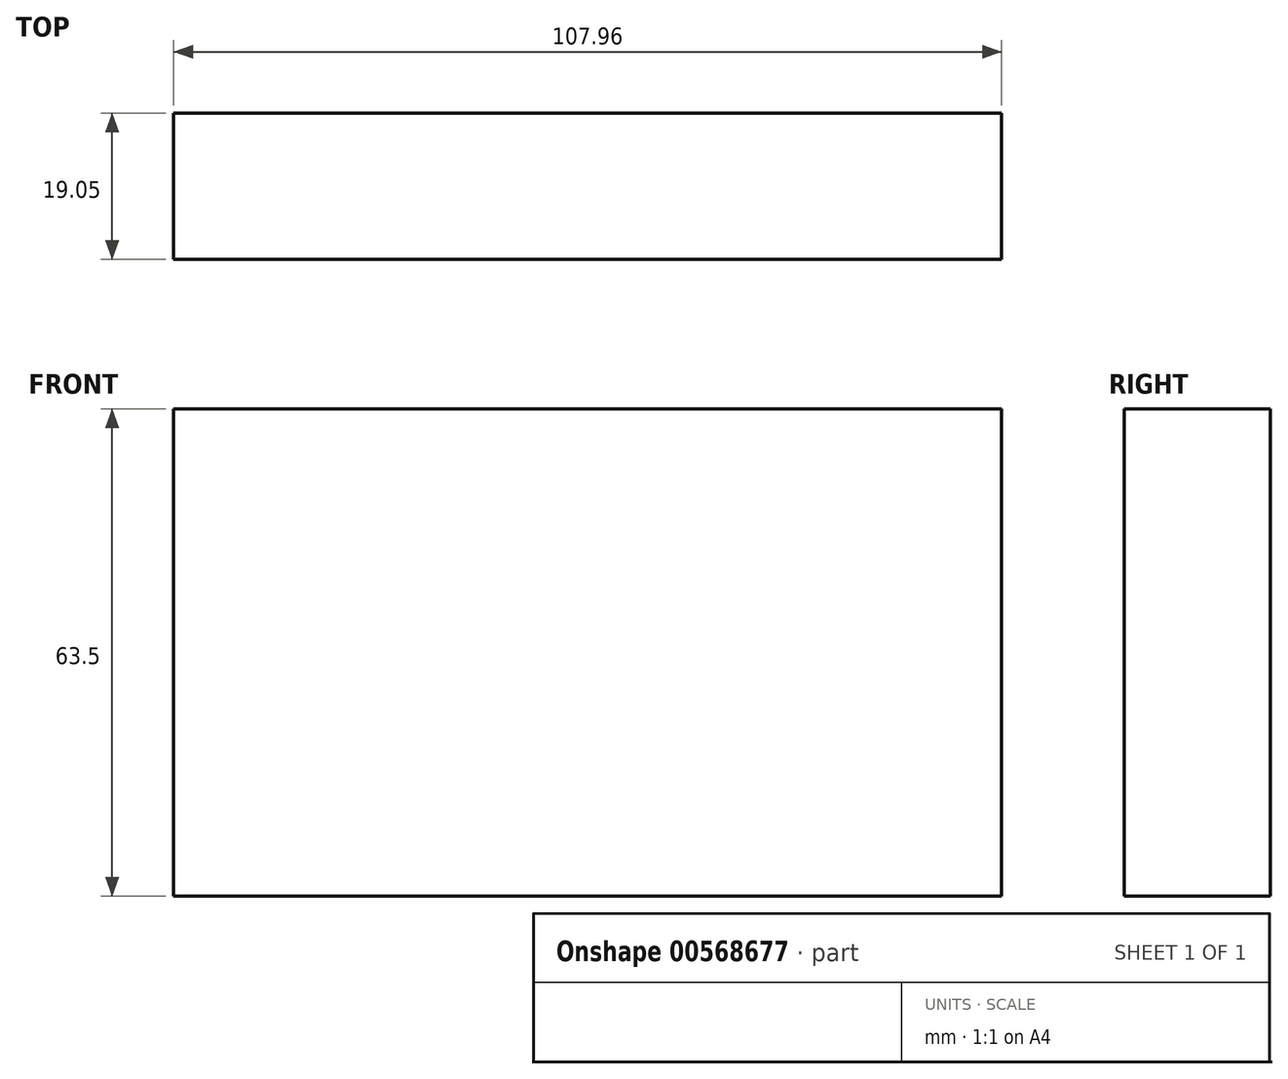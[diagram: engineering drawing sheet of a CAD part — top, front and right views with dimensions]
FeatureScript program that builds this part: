
annotation { "Feature Type Name" : "Feature", "Feature Type Description" : "" }
export const myFeature = defineFeature(function(context is Context, id is Id, definition is map)
    precondition{}
    {
        {
            var Q0;
            Q0=qCreatedBy(makeId("Front.planeOp"),FACE);
            var sketch = newSketch(context, id + "F0", { "sketchPlane" : qUnion([Q0])});
            skLineSegment(sketch, "E0.bottom", {"start": v(53.98, -31.75) * mm, "end": v(-53.98, -31.75) * mm});
            skLineSegment(sketch, "E0.top", {"start": v(53.98, 31.75) * mm, "end": v(-53.98, 31.75) * mm});
            skLineSegment(sketch, "E0.left", {"start": v(53.98, -31.75) * mm, "end": v(53.98, 31.75) * mm});
            skLineSegment(sketch, "E0.right", {"start": v(-53.98, -31.75) * mm, "end": v(-53.98, 31.75) * mm});
            skPoint(sketch, "E0.middle", {"position": v(0, 0) * mm});
            skSolve(sketch);
        }
        {
            var Q0;
            Q0=makeQuery(id+"F0.imprint","IMPRINT",FACE,{"disambiguationData":[TD([[makeQuery(id+"F0.imprint","IMPRINT",EDGE,{"derivedFrom":sQuery(id+"F0.wireOp",EDGE,"E0.bottom")}),-1.0]])]});
            extrude(context, id + "F1", {"entities" : qUnion([Q0]), "depth" : 19.05 * mm, "offsetDistance" : 25.4 * mm});
        }
    });
